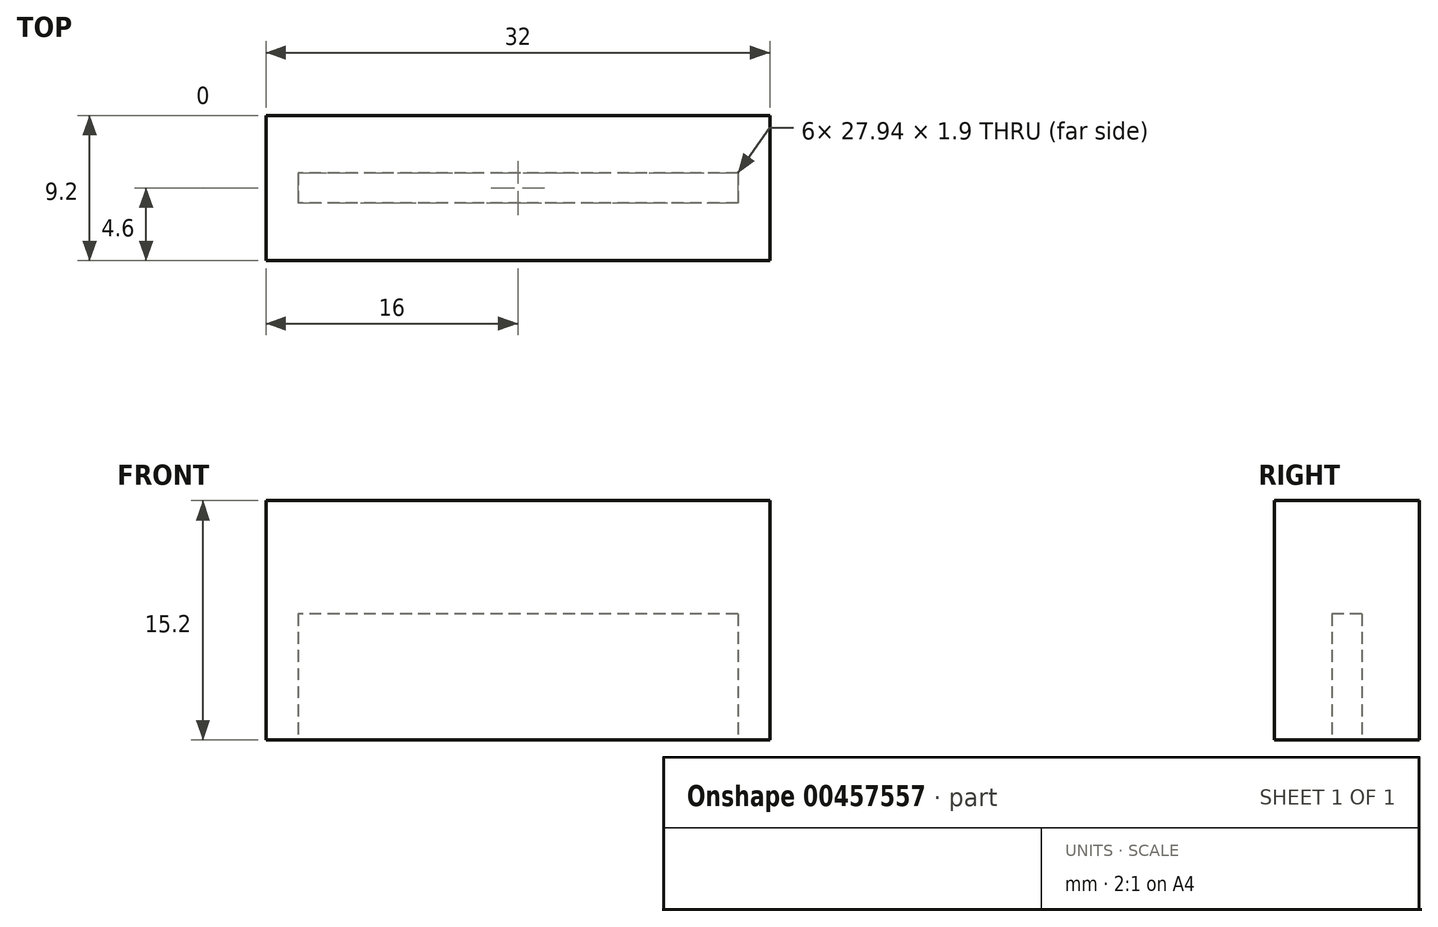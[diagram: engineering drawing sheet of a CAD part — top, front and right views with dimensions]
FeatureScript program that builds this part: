
annotation { "Feature Type Name" : "Feature", "Feature Type Description" : "" }
export const myFeature = defineFeature(function(context is Context, id is Id, definition is map)
    precondition{}
    {
        {
            var Q0;
            Q0=qCreatedBy(makeId("Front.planeOp"),FACE);
            var sketch = newSketch(context, id + "F0", { "sketchPlane" : qUnion([Q0])});
            skLineSegment(sketch, "E0.bottom", {"start": v(16, -7.6) * mm, "end": v(-16, -7.6) * mm});
            skLineSegment(sketch, "E0.top", {"start": v(16, 7.6) * mm, "end": v(-16, 7.6) * mm});
            skLineSegment(sketch, "E0.left", {"start": v(16, -7.6) * mm, "end": v(16, 7.6) * mm});
            skLineSegment(sketch, "E0.right", {"start": v(-16, -7.6) * mm, "end": v(-16, 7.6) * mm});
            skPoint(sketch, "E0.middle", {"position": v(0, 0) * mm});
            skSolve(sketch);
        }
        {
            var Q0;
            Q0 = qSketchRegion(id + "F0", true);
            extrude(context, id + "F1", {"entities" : qUnion([Q0]), "endBound" : BoundingType.SYMMETRIC, "depth" : 9.2 * mm});
        }
        {
            var Q0;
            Q0=makeQuery(id+"F1.opExtrude","SWEPT_FACE",FACE,{"disambiguationData":[OSD([sQuery(id+"F0.wireOp",EDGE,"E0.bottom")])]});
            var sketch = newSketch(context, id + "F2", { "sketchPlane" : qUnion([Q0])});
            skLineSegment(sketch, "E1.bottom", {"start": v(13.97, -0.95) * mm, "end": v(-13.97, -0.95) * mm});
            skLineSegment(sketch, "E1.top", {"start": v(13.97, 0.95) * mm, "end": v(-13.97, 0.95) * mm});
            skLineSegment(sketch, "E1.left", {"start": v(13.97, -0.95) * mm, "end": v(13.97, 0.95) * mm});
            skLineSegment(sketch, "E1.right", {"start": v(-13.97, -0.95) * mm, "end": v(-13.97, 0.95) * mm});
            skPoint(sketch, "E1.middle", {"position": v(0, 0) * mm});
            skSolve(sketch);
        }
        {
            var Q0;
            Q0 = qSketchRegion(id + "F2", true);
            extrude(context, id + "F3", {"entities" : qUnion([Q0]), "operationType" : NewBodyOperationType.REMOVE, "oppositeDirection" : true, "depth" : 8 * mm});
        }
    });
